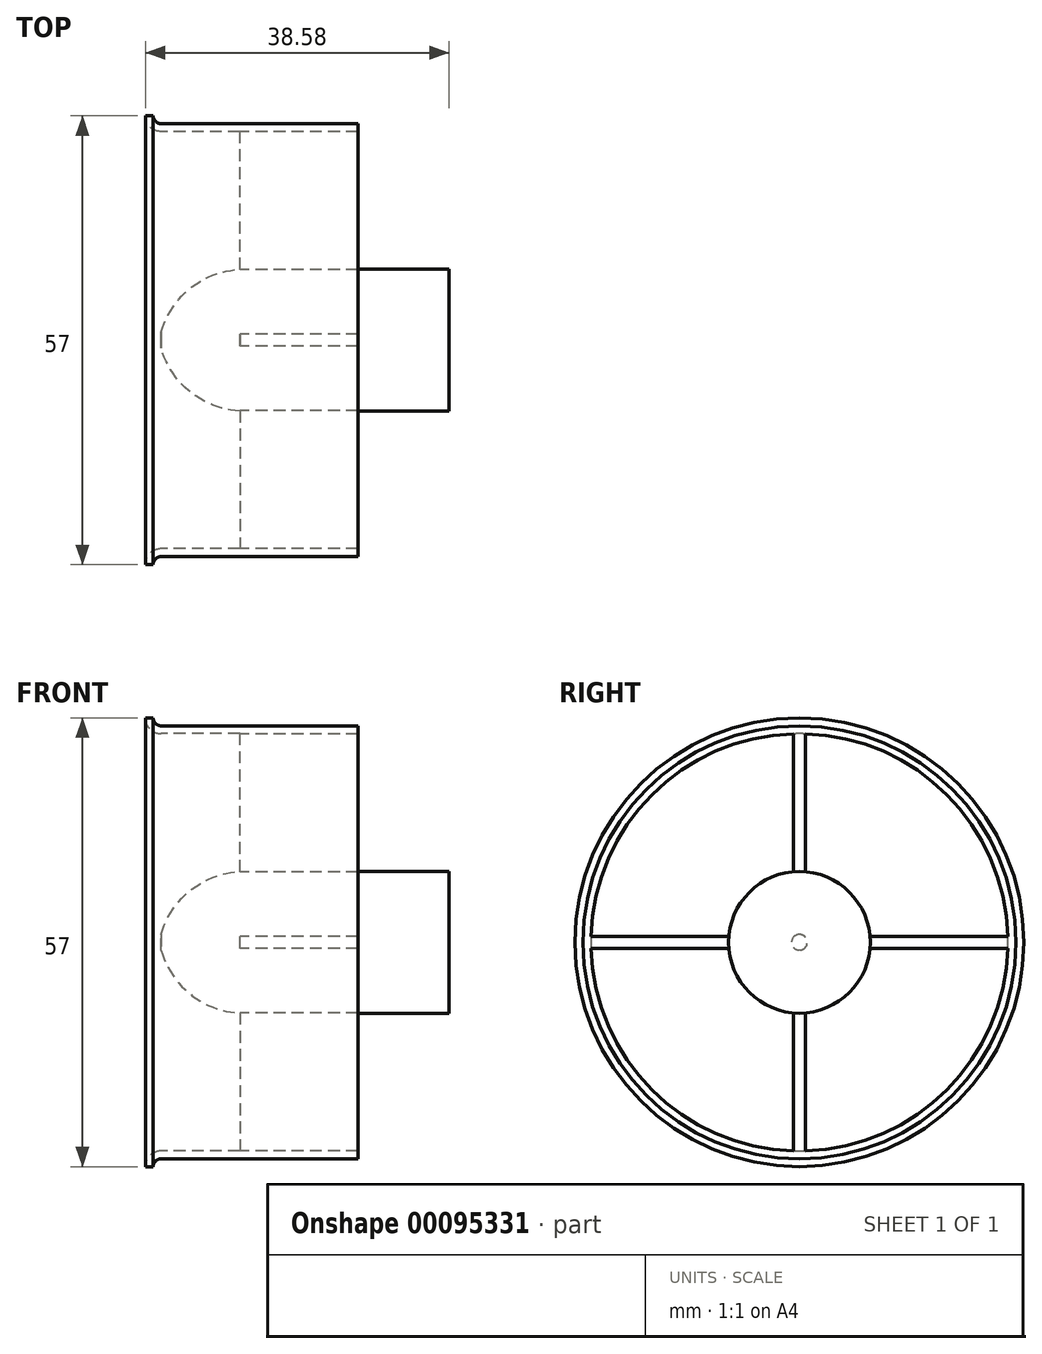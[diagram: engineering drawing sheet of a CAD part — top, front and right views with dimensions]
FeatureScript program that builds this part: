
annotation { "Feature Type Name" : "Feature", "Feature Type Description" : "" }
export const myFeature = defineFeature(function(context is Context, id is Id, definition is map)
    precondition{}
    {
        {
            var Q0;
            Q0=qCreatedBy(makeId("Front.planeOp"),FACE);
            var sketch = newSketch(context, id + "F0", { "sketchPlane" : qUnion([Q0])});
            skLineSegment(sketch, "E0", {"start": v(0, 26.5) * mm, "end": v(25, 26.5) * mm});
            skLineSegment(sketch, "E1", {"start": v(25, 26.5) * mm, "end": v(25, 27.5) * mm});
            skLineSegment(sketch, "E2", {"start": v(25, 27.5) * mm, "end": v(0, 27.5) * mm});
            skArc(sketch, "E3", {"start": v(-2, 28.5) * mm, "mid": v(-1.41, 27.09) * mm, "end": v(0, 26.5) * mm});
            skLineSegment(sketch, "E4", {"start": v(0, 0) * mm, "end": v(39.33, 0) * mm, "construction": true});
            skArc(sketch, "E5", {"start": v(-1, 28.5) * mm, "mid": v(-0.7, 27.8) * mm, "end": v(0, 27.5) * mm});
            skLineSegment(sketch, "E6", {"start": v(-2, 28.5) * mm, "end": v(-1, 28.5) * mm});
            skLineSegment(sketch, "E7", {"start": v(0, 0) * mm, "end": v(0, 1) * mm});
            skArc(sketch, "E8", {"start": v(10.58, 9) * mm, "mid": v(3.95, 6.77) * mm, "end": v(0, 1) * mm});
            skLineSegment(sketch, "E9", {"start": v(10.58, 9) * mm, "end": v(36.58, 9) * mm});
            skLineSegment(sketch, "E10", {"start": v(36.58, 9) * mm, "end": v(36.58, 0) * mm});
            skLineSegment(sketch, "E11", {"start": v(36.58, 0) * mm, "end": v(0, 0) * mm});
            skSolve(sketch);
        }
        {
            var Q0;
            Q0 = qSketchRegion(id + "F0", true);
            var Q1;
            Q1=sQuery(id+"F0.wireOp",EDGE,"E4");
            revolve(context, id + "F1", {"entities" : qUnion([Q0]), "axis" : qUnion([Q1]), "revolveType" : RevolveType.FULL});
        }
        {
            var Q0;
            Q0=qCreatedBy(makeId("Right.planeOp"),FACE);
            var sketch = newSketch(context, id + "F2", { "sketchPlane" : qUnion([Q0])});
            skLineSegment(sketch, "E12.bottom", {"start": v(0.75, 8) * mm, "end": v(-0.75, 8) * mm});
            skLineSegment(sketch, "E12.top", {"start": v(0.75, 27) * mm, "end": v(-0.75, 27) * mm});
            skLineSegment(sketch, "E12.left", {"start": v(-0.75, 8) * mm, "end": v(-0.75, 27) * mm});
            skLineSegment(sketch, "E12.right", {"start": v(0.75, 8) * mm, "end": v(0.75, 27) * mm});
            skLineSegment(sketch, "E13", {"start": v(0, 8) * mm, "end": v(0, 0) * mm, "construction": true});
            skLineSegment(sketch, "E14.1.0", {"start": v(-8, 0.75) * mm, "end": v(-27, 0.75) * mm});
            skLineSegment(sketch, "E14.1.1", {"start": v(-8, -0.75) * mm, "end": v(-27, -0.75) * mm});
            skLineSegment(sketch, "E14.1.2", {"start": v(-27, 0.75) * mm, "end": v(-27, -0.75) * mm});
            skLineSegment(sketch, "E14.1.3", {"start": v(-8, 0.75) * mm, "end": v(-8, -0.75) * mm});
            skLineSegment(sketch, "E14.2.0", {"start": v(-0.75, -8) * mm, "end": v(-0.75, -27) * mm});
            skLineSegment(sketch, "E14.2.1", {"start": v(0.75, -8) * mm, "end": v(0.75, -27) * mm});
            skLineSegment(sketch, "E14.2.2", {"start": v(-0.75, -27) * mm, "end": v(0.75, -27) * mm});
            skLineSegment(sketch, "E14.2.3", {"start": v(-0.75, -8) * mm, "end": v(0.75, -8) * mm});
            skLineSegment(sketch, "E14.3.0", {"start": v(8, -0.75) * mm, "end": v(27, -0.75) * mm});
            skLineSegment(sketch, "E14.3.1", {"start": v(8, 0.75) * mm, "end": v(27, 0.75) * mm});
            skLineSegment(sketch, "E14.3.2", {"start": v(27, -0.75) * mm, "end": v(27, 0.75) * mm});
            skLineSegment(sketch, "E14.3.3", {"start": v(8, -0.75) * mm, "end": v(8, 0.75) * mm});
            skPoint(sketch, "E14.center", {"position": v(0, 0) * mm});
            skSolve(sketch);
        }
        {
            var Q0;
            Q0=makeQuery(id+"F2.imprint","IMPRINT",FACE,{"disambiguationData":[TD([[makeQuery(id+"F2.imprint","IMPRINT",EDGE,{"derivedFrom":sQuery(id+"F2.wireOp",EDGE,"E12.bottom")}),-1.0]])]});
            var Q1;
            Q1=makeQuery(id+"F2.imprint","IMPRINT",FACE,{"disambiguationData":[TD([[makeQuery(id+"F2.imprint","IMPRINT",EDGE,{"derivedFrom":sQuery(id+"F2.wireOp",EDGE,"E14.1.0")}),1.0]])]});
            var Q2;
            Q2=makeQuery(id+"F2.imprint","IMPRINT",FACE,{"disambiguationData":[TD([[makeQuery(id+"F2.imprint","IMPRINT",EDGE,{"derivedFrom":sQuery(id+"F2.wireOp",EDGE,"E14.2.0")}),1.0]])]});
            var Q3;
            Q3=makeQuery(id+"F2.imprint","IMPRINT",FACE,{"disambiguationData":[TD([[makeQuery(id+"F2.imprint","IMPRINT",EDGE,{"derivedFrom":sQuery(id+"F2.wireOp",EDGE,"E14.3.0")}),1.0]])]});
            extrude(context, id + "F3", {"entities" : qUnion([Q0, Q1, Q2, Q3]), "operationType" : NewBodyOperationType.ADD, "depth" : 25 * mm, "hasSecondDirection" : true, "secondDirectionOppositeDirection" : false, "secondDirectionDepth" : 10 * mm});
        }
    });
